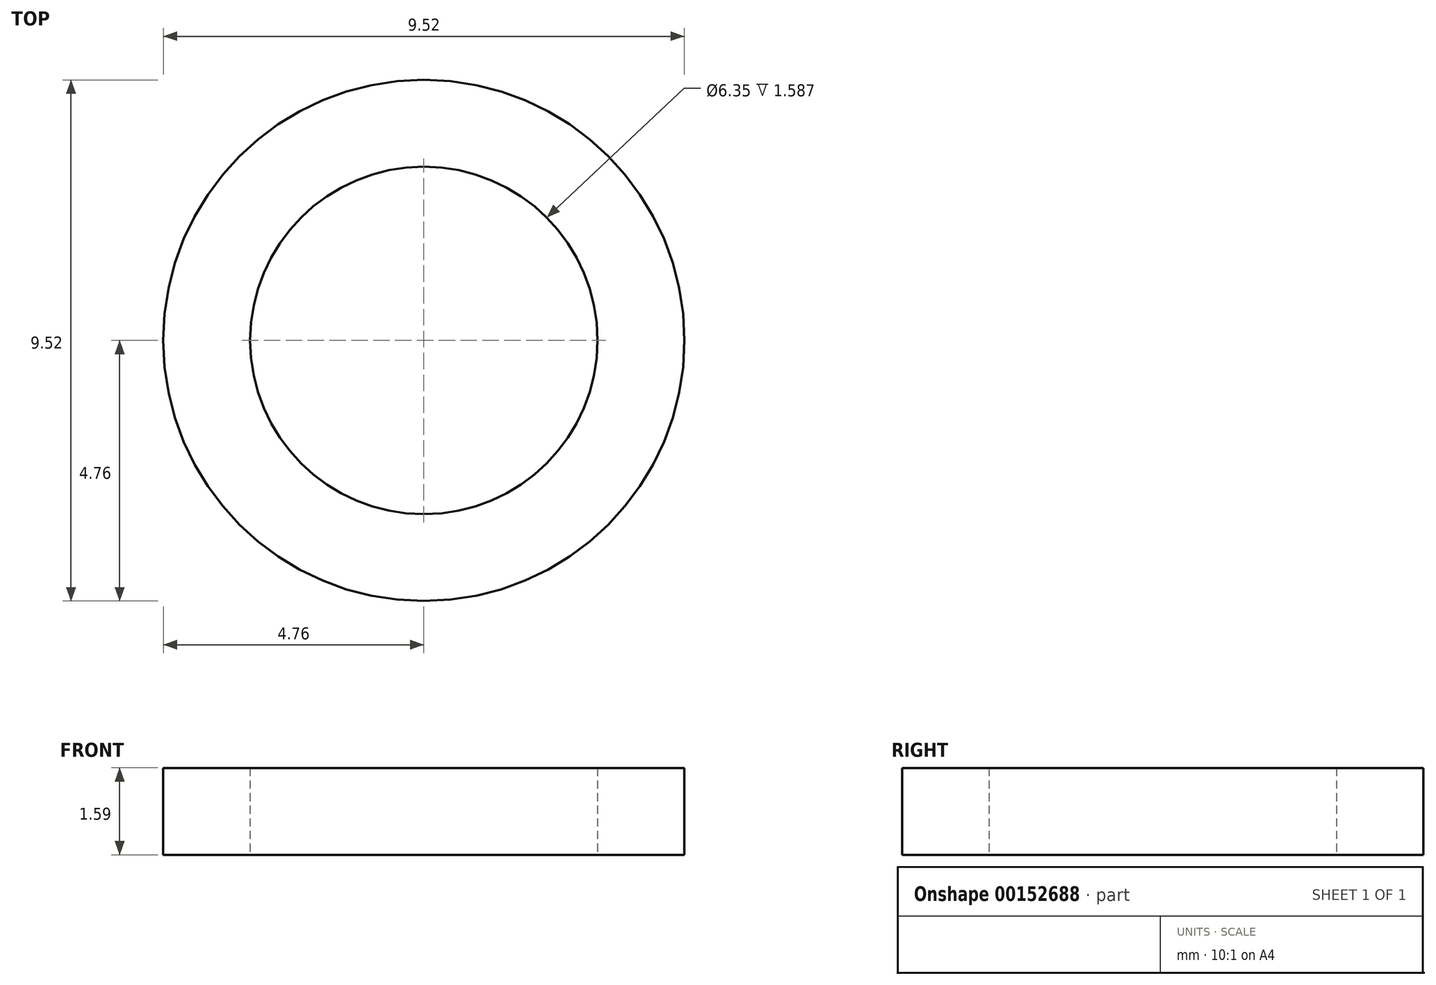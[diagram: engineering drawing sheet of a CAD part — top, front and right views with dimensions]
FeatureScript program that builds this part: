
annotation { "Feature Type Name" : "Feature", "Feature Type Description" : "" }
export const myFeature = defineFeature(function(context is Context, id is Id, definition is map)
    precondition{}
    {
        {
            var Q0;
            Q0=qCreatedBy(makeId("Top.planeOp"),FACE);
            var sketch = newSketch(context, id + "F0", { "sketchPlane" : qUnion([Q0])});
            skCircle(sketch, "E0", {"center": v(0, 0) * mm, "radius": 3.18 * mm});
            skCircle(sketch, "E1", {"center": v(0, 0) * mm, "radius": 4.76 * mm});
            skSolve(sketch);
        }
        {
            var Q0;
            Q0=qSketchRegion(id+"F0",true);
            extrude(context, id + "F1", {"entities" : qUnion([Q0]), "depth" : 1.59 * mm});
        }
    });
